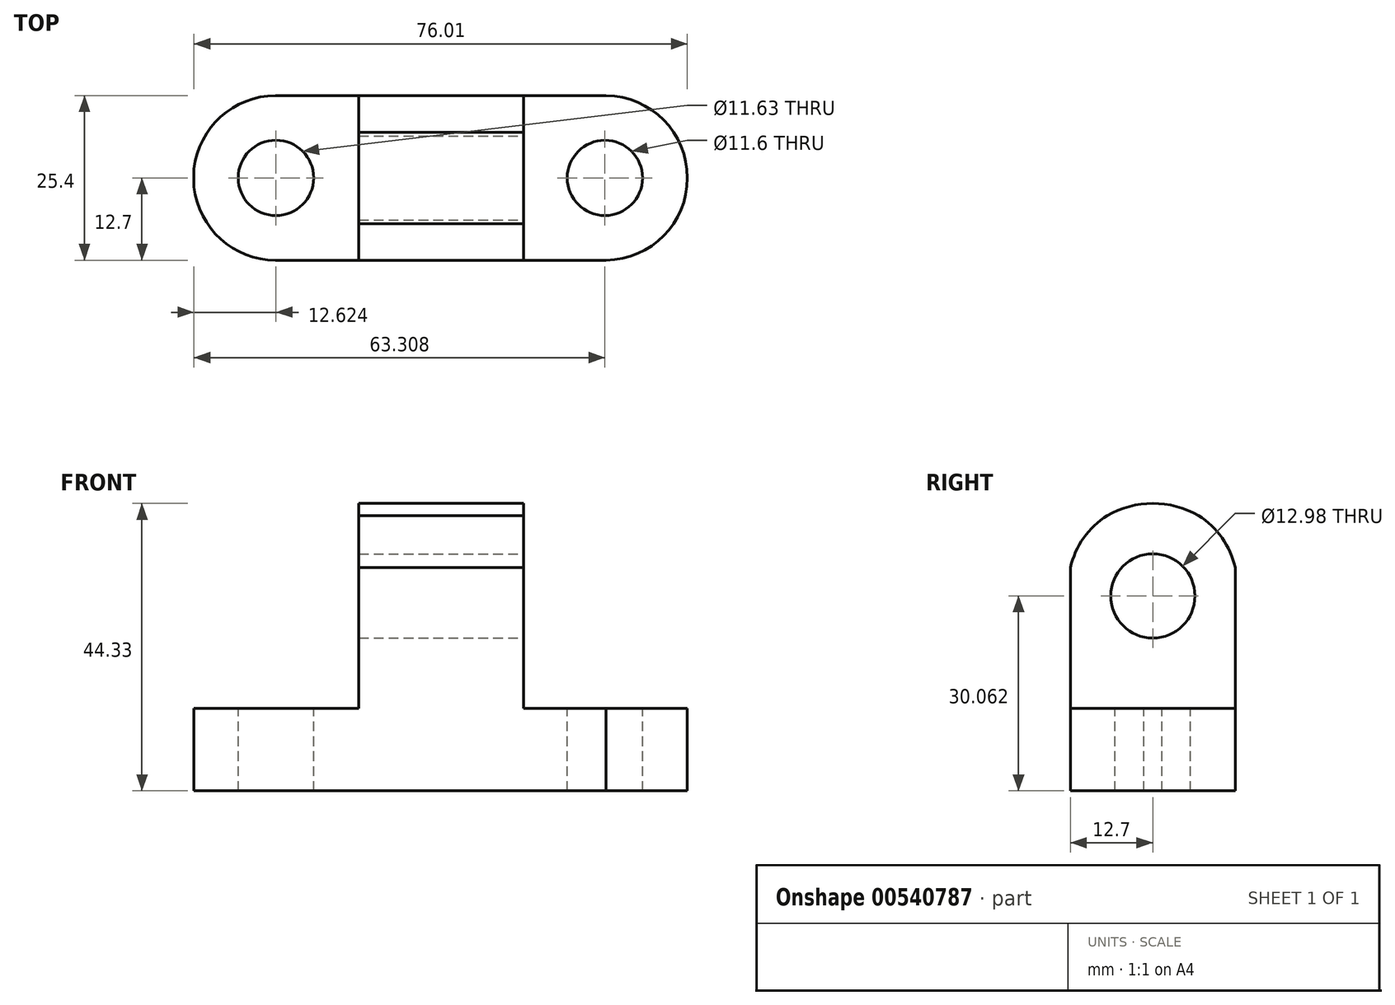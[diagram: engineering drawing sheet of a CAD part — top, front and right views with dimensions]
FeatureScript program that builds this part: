
annotation { "Feature Type Name" : "Feature", "Feature Type Description" : "" }
export const myFeature = defineFeature(function(context is Context, id is Id, definition is map)
    precondition{}
    {
        {
            var Q0;
            Q0=qCreatedBy(makeId("Front.planeOp"),FACE);
            var sketch = newSketch(context, id + "F0", { "sketchPlane" : qUnion([Q0])});
            skLineSegment(sketch, "E0", {"start": v(0, 0) * mm, "end": v(0, 12.7) * mm});
            skLineSegment(sketch, "E1", {"start": v(0, 12.7) * mm, "end": v(25.4, 12.7) * mm});
            skLineSegment(sketch, "E2", {"start": v(25.4, 12.7) * mm, "end": v(25.4, 44.45) * mm});
            skLineSegment(sketch, "E3", {"start": v(25.4, 44.45) * mm, "end": v(50.8, 44.45) * mm});
            skLineSegment(sketch, "E4", {"start": v(50.8, 44.45) * mm, "end": v(50.8, 12.7) * mm});
            skLineSegment(sketch, "E5", {"start": v(50.8, 12.7) * mm, "end": v(76.2, 12.7) * mm});
            skLineSegment(sketch, "E6", {"start": v(76.2, 12.7) * mm, "end": v(76.2, 0) * mm});
            skLineSegment(sketch, "E7", {"start": v(76.2, 0) * mm, "end": v(0, 0) * mm});
            skSolve(sketch);
        }
        {
            var Q0;
            Q0=makeQuery(id+"F0.imprint","IMPRINT",FACE,{"disambiguationData":[TD([[makeQuery(id+"F0.imprint","IMPRINT",EDGE,{"derivedFrom":sQuery(id+"F0.wireOp",EDGE,"E0")}),-1.0]])]});
            extrude(context, id + "F1", {"entities" : qUnion([Q0]), "depth" : 25.4 * mm, "offsetDistance" : 25.4 * mm});
        }
        {
            var Q0;
            Q0=makeQuery(id+"F1.opExtrude","SWEPT_FACE",FACE,{"disambiguationData":[OSD([sQuery(id+"F0.wireOp",EDGE,"E5")])]});
            var sketch = newSketch(context, id + "F2", { "sketchPlane" : qUnion([Q0])});
            skArc(sketch, "E8", {"start": v(63.5, -25.4) * mm, "mid": v(76, -12.7) * mm, "end": v(63.5, 0) * mm});
            skSolve(sketch);
        }
        {
            var Q0;
            {var subQ0=sQuery(id+"F2.wireOp",EDGE,"E8");Q0=makeQuery(id+"F2.imprint","IMPRINT",FACE,{"disambiguationData":[TD([[makeQuery(id+"F2.imprint","IMPRINT",EDGE,{"derivedFrom":subQ0}),-1.0]])]});}
            extrude(context, id + "F3", {"entities" : qUnion([Q0]), "operationType" : NewBodyOperationType.REMOVE, "oppositeDirection" : true, "depth" : 25.4 * mm, "offsetDistance" : 25.4 * mm});
        }
        {
            var Q0;
            Q0=makeQuery(id+"F1.opExtrude","SWEPT_FACE",FACE,{"disambiguationData":[OSD([sQuery(id+"F0.wireOp",EDGE,"E1")])]});
            var sketch = newSketch(context, id + "F4", { "sketchPlane" : qUnion([Q0])});
            skLineSegment(sketch, "E9", {"start": v(25.4, -12.7) * mm, "end": v(0, -12.7) * mm});
            skArc(sketch, "E10", {"start": v(12.7, 0) * mm, "mid": v(-0.08, -12.7) * mm, "end": v(12.7, -25.4) * mm});
            skSolve(sketch);
        }
        {
            var Q0;
            {var subQ0=sQuery(id+"F4.wireOp",EDGE,"E10");var subQ1=sQuery(id+"F0.wireOp",EDGE,"E1");var subQ2=makeQuery(id+"F1.opExtrude","CAP_EDGE",EDGE,{"disambiguationData":[OSD([subQ1])],"isStart":true});var subQ3=makeQuery(id+"F4.imprint","INTERSECT",VERTEX,{"disambiguationData":[OD(1.0)],"derivedFrom":[subQ2,subQ0]});Q0=makeQuery(id+"F4.imprint","IMPRINT",FACE,{"disambiguationData":[TD([[makeQuery(id+"F4.imprint","IMPRINT",EDGE,{"disambiguationData":[TD([[subQ3,-1.0]])],"derivedFrom":subQ0}),-1.0]])]});}
            var Q1;
            {var subQ0=sQuery(id+"F4.wireOp",EDGE,"E10");var subQ1=sQuery(id+"F0.wireOp",EDGE,"E1");var subQ4=makeQuery(id+"F1.opExtrude","CAP_EDGE",EDGE,{"disambiguationData":[OSD([subQ1])],"isStart":false});var subQ5=makeQuery(id+"F4.imprint","INTERSECT",VERTEX,{"disambiguationData":[OD(1.0)],"derivedFrom":[subQ4,subQ0]});Q1=makeQuery(id+"F4.imprint","IMPRINT",FACE,{"disambiguationData":[TD([[makeQuery(id+"F4.imprint","IMPRINT",EDGE,{"disambiguationData":[TD([[subQ5,1.0]])],"derivedFrom":subQ0}),-1.0]])]});}
            extrude(context, id + "F5", {"entities" : qUnion([Q0, Q1]), "operationType" : NewBodyOperationType.REMOVE, "oppositeDirection" : true, "depth" : 25.4 * mm, "offsetDistance" : 25.4 * mm});
        }
        {
            var Q0;
            Q0=makeQuery(id+"F1.opExtrude","SWEPT_FACE",FACE,{"disambiguationData":[OSD([sQuery(id+"F0.wireOp",EDGE,"E1")])]});
            var sketch = newSketch(context, id + "F6", { "sketchPlane" : qUnion([Q0])});
            skCircle(sketch, "E11", {"center": v(12.62, -12.7) * mm, "radius": 6.35 * mm});
            skLineSegment(sketch, "E12", {"start": v(12.62, -12.7) * mm, "end": v(18.97, -12.7) * mm});
            skSolve(sketch);
        }
        {
            var Q0;
            Q0=makeQuery(id+"F6.imprint","IMPRINT",FACE,{"disambiguationData":[TD([[makeQuery(id+"F6.imprint","IMPRINT",EDGE,{"derivedFrom":sQuery(id+"F6.wireOp",EDGE,"E11")}),1.0]])]});
            extrude(context, id + "F7", {"entities" : qUnion([Q0]), "operationType" : NewBodyOperationType.REMOVE, "depth" : 25.4 * mm, "offsetDistance" : 25.4 * mm});
        }
        {
            var Q0;
            Q0=makeQuery(id+"F1.opExtrude","SWEPT_FACE",FACE,{"disambiguationData":[OSD([sQuery(id+"F0.wireOp",EDGE,"E1")])]});
            var sketch = newSketch(context, id + "F8", { "sketchPlane" : qUnion([Q0])});
            skCircle(sketch, "E13", {"center": v(12.62, -12.7) * mm, "radius": 6.35 * mm});
            skSolve(sketch);
        }
        {
            var Q0;
            Q0=makeQuery(id+"F1.opExtrude","SWEPT_FACE",FACE,{"disambiguationData":[OSD([sQuery(id+"F0.wireOp",EDGE,"E5")])]});
            var sketch = newSketch(context, id + "F9", { "sketchPlane" : qUnion([Q0])});
            skCircle(sketch, "E14", {"center": v(63.3, -12.7) * mm, "radius": 6.31 * mm});
            skSolve(sketch);
        }
        {
            var Q0;
            Q0=makeQuery(id+"F8.imprint","IMPRINT",FACE,{"disambiguationData":[TD([[makeQuery(id+"F8.imprint","IMPRINT",EDGE,{"derivedFrom":sQuery(id+"F8.wireOp",EDGE,"E13")}),1.0]])]});
            var Q1;
            Q1=makeQuery(id+"F9.imprint","IMPRINT",FACE,{"disambiguationData":[TD([[makeQuery(id+"F9.imprint","IMPRINT",EDGE,{"derivedFrom":sQuery(id+"F9.wireOp",EDGE,"E14")}),1.0]])]});
            extrude(context, id + "F10", {"entities" : qUnion([Q0, Q1]), "operationType" : NewBodyOperationType.REMOVE, "depth" : 254 * mm, "offsetDistance" : 25.4 * mm});
        }
        {
            var Q0;
            Q0=makeQuery(id+"F1.opExtrude","SWEPT_FACE",FACE,{"disambiguationData":[OSD([sQuery(id+"F0.wireOp",EDGE,"E1")])]});
            var sketch = newSketch(context, id + "F11", { "sketchPlane" : qUnion([Q0])});
            skCircle(sketch, "E15", {"center": v(12.62, -12.7) * mm, "radius": 5.81 * mm});
            skLineSegment(sketch, "E16", {"start": v(12.62, -12.7) * mm, "end": v(0, -14.08) * mm});
            skSolve(sketch);
        }
        {
            var Q0;
            Q0=makeQuery(id+"F11.imprint","IMPRINT",FACE,{"disambiguationData":[TD([[makeQuery(id+"F11.imprint","IMPRINT",EDGE,{"derivedFrom":sQuery(id+"F11.wireOp",EDGE,"E15")}),1.0]])]});
            extrude(context, id + "F12", {"entities" : qUnion([Q0]), "operationType" : NewBodyOperationType.REMOVE, "oppositeDirection" : true, "depth" : 25.4 * mm, "offsetDistance" : 25.4 * mm});
        }
        {
            var Q0;
            Q0=makeQuery(id+"F1.opExtrude","SWEPT_FACE",FACE,{"disambiguationData":[OSD([sQuery(id+"F0.wireOp",EDGE,"E5")])]});
            var sketch = newSketch(context, id + "F13", { "sketchPlane" : qUnion([Q0])});
            skCircle(sketch, "E17", {"center": v(63.3, -12.7) * mm, "radius": 5.8 * mm});
            skSolve(sketch);
        }
        {
            var Q0;
            Q0=makeQuery(id+"F13.imprint","IMPRINT",FACE,{"disambiguationData":[TD([[makeQuery(id+"F13.imprint","IMPRINT",EDGE,{"derivedFrom":sQuery(id+"F13.wireOp",EDGE,"E17")}),1.0]])]});
            extrude(context, id + "F14", {"entities" : qUnion([Q0]), "operationType" : NewBodyOperationType.REMOVE, "depth" : 25.4 * mm, "offsetDistance" : 25.4 * mm});
        }
        {
            var Q0;
            Q0=makeQuery(id+"F13.imprint","IMPRINT",FACE,{"disambiguationData":[TD([[makeQuery(id+"F13.imprint","IMPRINT",EDGE,{"derivedFrom":sQuery(id+"F13.wireOp",EDGE,"E17")}),1.0]])]});
            extrude(context, id + "F15", {"entities" : qUnion([Q0]), "operationType" : NewBodyOperationType.REMOVE, "oppositeDirection" : true, "depth" : 254 * mm, "offsetDistance" : 25.4 * mm});
        }
        {
            var Q0;
            Q0=makeQuery(id+"F1.opExtrude","SWEPT_FACE",FACE,{"disambiguationData":[OSD([sQuery(id+"F0.wireOp",EDGE,"E4")])]});
            var sketch = newSketch(context, id + "F16", { "sketchPlane" : qUnion([Q0])});
            skLineSegment(sketch, "E18", {"start": v(-12.7, 12.7) * mm, "end": v(-12.7, 44.45) * mm});
            skArc(sketch, "E19", {"start": v(0, 28.57) * mm, "mid": v(-12.7, 44.53) * mm, "end": v(-25.4, 28.57) * mm});
            skLineSegment(sketch, "E20", {"start": v(-12.7, 31.5) * mm, "end": v(-25.4, 31.5) * mm});
            skSolve(sketch);
        }
        {
            var Q0;
            {var subQ0=sQuery(id+"F16.wireOp",EDGE,"E19");var subQ1=sQuery(id+"F0.wireOp",EDGE,"E4");var subQ4=makeQuery(id+"F1.opExtrude","CAP_EDGE",EDGE,{"disambiguationData":[OSD([subQ1])],"isStart":false});var subQ5=makeQuery(id+"F16.imprint","INTERSECT",VERTEX,{"disambiguationData":[OD(1.0)],"derivedFrom":[subQ4,subQ0]});Q0=makeQuery(id+"F16.imprint","IMPRINT",FACE,{"disambiguationData":[TD([[makeQuery(id+"F16.imprint","IMPRINT",EDGE,{"disambiguationData":[TD([[subQ5,1.0]])],"derivedFrom":subQ0}),-1.0]])]});}
            var Q1;
            {var subQ0=sQuery(id+"F16.wireOp",EDGE,"E19");var subQ1=sQuery(id+"F0.wireOp",EDGE,"E4");var subQ2=makeQuery(id+"F1.opExtrude","CAP_EDGE",EDGE,{"disambiguationData":[OSD([subQ1])],"isStart":true});var subQ3=makeQuery(id+"F16.imprint","INTERSECT",VERTEX,{"disambiguationData":[OD(1.0)],"derivedFrom":[subQ2,subQ0]});Q1=makeQuery(id+"F16.imprint","IMPRINT",FACE,{"disambiguationData":[TD([[makeQuery(id+"F16.imprint","IMPRINT",EDGE,{"disambiguationData":[TD([[subQ3,-1.0]])],"derivedFrom":subQ0}),-1.0]])]});}
            extrude(context, id + "F17", {"entities" : qUnion([Q0, Q1]), "operationType" : NewBodyOperationType.REMOVE, "oppositeDirection" : true, "depth" : 25.4 * mm, "offsetDistance" : 25.4 * mm});
        }
        {
            var Q0;
            Q0=makeQuery(id+"F1.opExtrude","SWEPT_FACE",FACE,{"disambiguationData":[OSD([sQuery(id+"F0.wireOp",EDGE,"E4")])]});
            var sketch = newSketch(context, id + "F18", { "sketchPlane" : qUnion([Q0])});
            skCircle(sketch, "E21", {"center": v(-12.7, 31.84) * mm, "radius": 6.3 * mm});
            skSolve(sketch);
        }
        {
            var Q0;
            Q0=makeQuery(id+"F18.imprint","IMPRINT",FACE,{"disambiguationData":[TD([[makeQuery(id+"F18.imprint","IMPRINT",EDGE,{"derivedFrom":sQuery(id+"F18.wireOp",EDGE,"E21")}),1.0]])]});
            extrude(context, id + "F19", {"entities" : qUnion([Q0]), "operationType" : NewBodyOperationType.REMOVE, "depth" : 254 * mm, "offsetDistance" : 25.4 * mm});
        }
        {
            var Q0;
            Q0=makeQuery(id+"F1.opExtrude","SWEPT_FACE",FACE,{"disambiguationData":[OSD([sQuery(id+"F0.wireOp",EDGE,"E4")])]});
            var sketch = newSketch(context, id + "F20", { "sketchPlane" : qUnion([Q0])});
            skArc(sketch, "E22", {"start": v(0, 23.56) * mm, "mid": v(-12.7, 44.33) * mm, "end": v(-25.4, 23.56) * mm});
            skSolve(sketch);
        }
        {
            var Q0;
            {var subQ2=sQuery(id+"F0.wireOp",EDGE,"E4");var subQ3=makeQuery(id+"F1.opExtrude","SWEPT_EDGE",EDGE,{"disambiguationData":[OSD([sQuery(id+"F0.wireOp",EDGE,"E3"),subQ2])]});var subQ8=subQ3;Q0=makeQuery(id+"F20.imprint","IMPRINT",FACE,{"disambiguationData":[TD([[makeQuery(id+"F20.imprint","IMPRINT",EDGE,{"derivedFrom":subQ8}),-1.0]])]});}
            extrude(context, id + "F21", {"entities" : qUnion([Q0]), "operationType" : NewBodyOperationType.REMOVE, "oppositeDirection" : true, "depth" : 254 * mm, "offsetDistance" : 25.4 * mm});
        }
        {
            var Q0;
            Q0=makeQuery(id+"F1.opExtrude","SWEPT_FACE",FACE,{"disambiguationData":[OSD([sQuery(id+"F0.wireOp",EDGE,"E4")])]});
            var sketch = newSketch(context, id + "F22", { "sketchPlane" : qUnion([Q0])});
            skCircle(sketch, "E23", {"center": v(-12.7, 30.06) * mm, "radius": 6.5 * mm});
            skSolve(sketch);
        }
        {
            var Q0;
            Q0=makeQuery(id+"F22.imprint","IMPRINT",FACE,{"disambiguationData":[TD([[makeQuery(id+"F22.imprint","IMPRINT",EDGE,{"derivedFrom":sQuery(id+"F22.wireOp",EDGE,"E23")}),1.0]])]});
            extrude(context, id + "F23", {"entities" : qUnion([Q0]), "operationType" : NewBodyOperationType.REMOVE, "oppositeDirection" : true, "depth" : 25.4 * mm, "offsetDistance" : 25.4 * mm});
        }
    });
